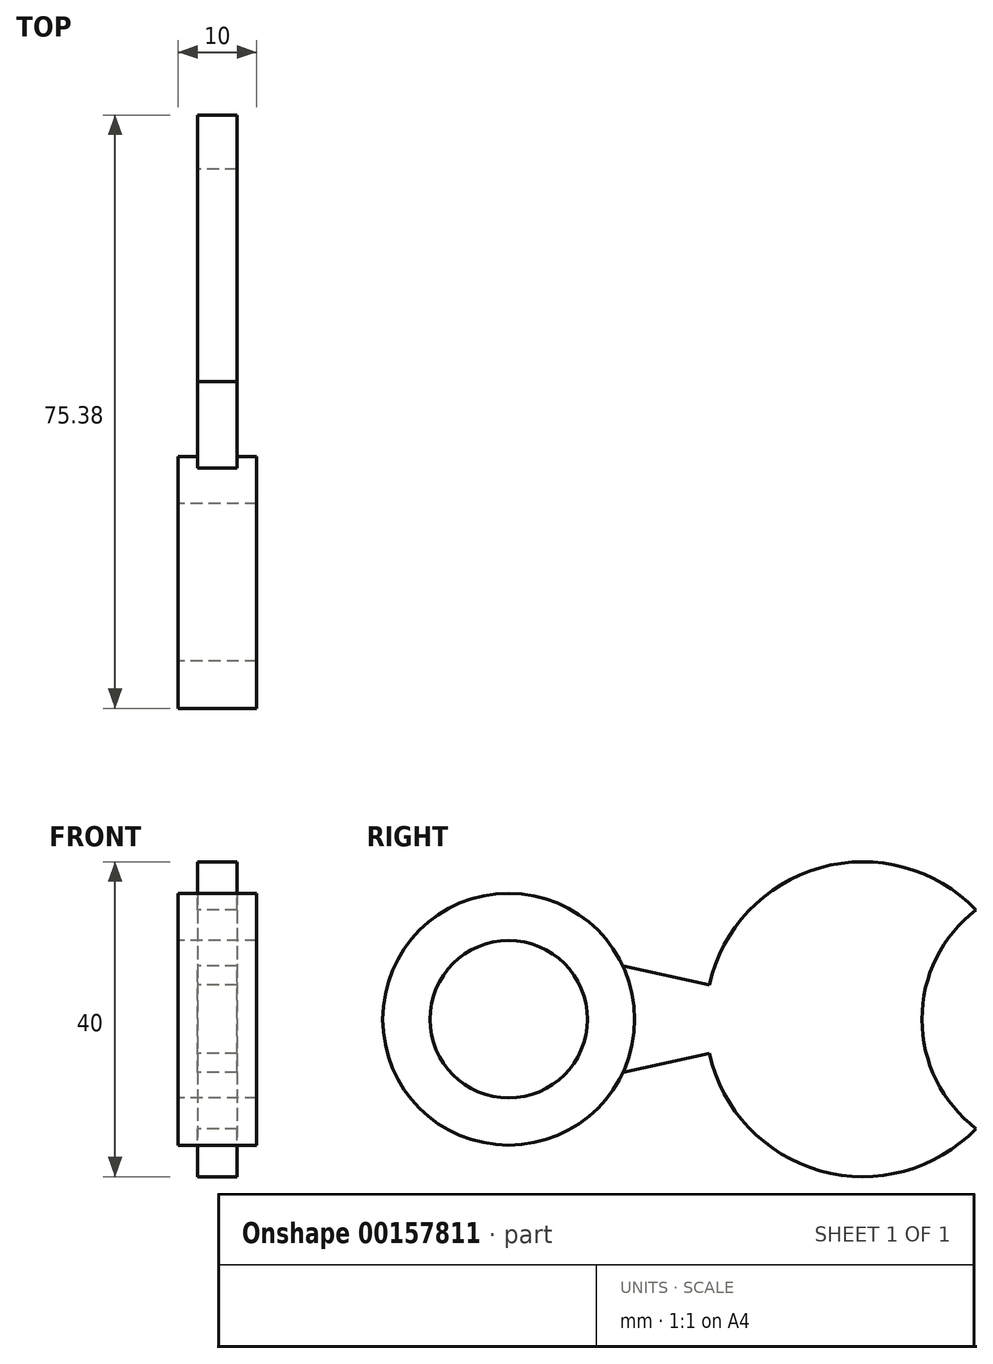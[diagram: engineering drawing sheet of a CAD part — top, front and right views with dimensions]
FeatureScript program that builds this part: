
annotation { "Feature Type Name" : "Feature", "Feature Type Description" : "" }
export const myFeature = defineFeature(function(context is Context, id is Id, definition is map)
    precondition{}
    {
        {
            var Q0;
            Q0=qCreatedBy(makeId("Right.planeOp"),FACE);
            var sketch = newSketch(context, id + "F0", { "sketchPlane" : qUnion([Q0])});
            skCircle(sketch, "E0", {"center": v(0, 0) * mm, "radius": 16 * mm});
            skCircle(sketch, "E1", {"center": v(0, 0) * mm, "radius": 10 * mm});
            skArc(sketch, "E2", {"start": v(59.38, 13.9) * mm, "mid": v(39.57, 19.25) * mm, "end": v(25.48, 4.34) * mm});
            skArc(sketch, "E3", {"start": v(59.37, 13.9) * mm, "mid": v(52.5, 0) * mm, "end": v(59.37, -13.9) * mm});
            skLineSegment(sketch, "E4.trimOffspring", {"start": v(14.5, 6.78) * mm, "end": v(25.48, 4.34) * mm});
            skLineSegment(sketch, "E5.trimOffspring", {"start": v(14.5, -6.78) * mm, "end": v(25.48, -4.34) * mm});
            skArc(sketch, "E6.trimOffspring", {"start": v(25.48, -4.34) * mm, "mid": v(39.57, -19.25) * mm, "end": v(59.38, -13.9) * mm});
            skSolve(sketch);
        }
        {
            var Q0;
            Q0=makeQuery(id+"F0.imprint","IMPRINT",FACE,{"disambiguationData":[TD([[makeQuery(id+"F0.imprint","IMPRINT",EDGE,{"derivedFrom":sQuery(id+"F0.wireOp",EDGE,"E1")}),1.0]])]});
            var Q1;
            Q1=makeQuery(id+"F0.imprint","IMPRINT",FACE,{"disambiguationData":[TD([[makeQuery(id+"F0.imprint","IMPRINT",EDGE,{"derivedFrom":sQuery(id+"F0.wireOp",EDGE,"E0")}),1.0]])]});
            extrude(context, id + "F1", {"entities" : qUnion([Q0, Q1]), "endBound" : BoundingType.SYMMETRIC, "depth" : 10 * mm});
        }
        {
            var Q0;
            Q0=makeQuery(id+"F0.imprint","IMPRINT",FACE,{"disambiguationData":[TD([[makeQuery(id+"F0.imprint","IMPRINT",EDGE,{"derivedFrom":sQuery(id+"F0.wireOp",EDGE,"E1")}),1.0]])]});
            extrude(context, id + "F2", {"entities" : qUnion([Q0]), "operationType" : NewBodyOperationType.REMOVE, "endBound" : BoundingType.SYMMETRIC, "depth" : 10 * mm});
        }
        {
            var Q0;
            Q0=makeQuery(id+"F0.imprint","IMPRINT",FACE,{"disambiguationData":[TD([[makeQuery(id+"F0.imprint","IMPRINT",EDGE,{"derivedFrom":sQuery(id+"F0.wireOp",EDGE,"E2")}),1.0]])]});
            extrude(context, id + "F3", {"entities" : qUnion([Q0]), "operationType" : NewBodyOperationType.ADD, "endBound" : BoundingType.SYMMETRIC, "depth" : 5 * mm});
        }
    });
